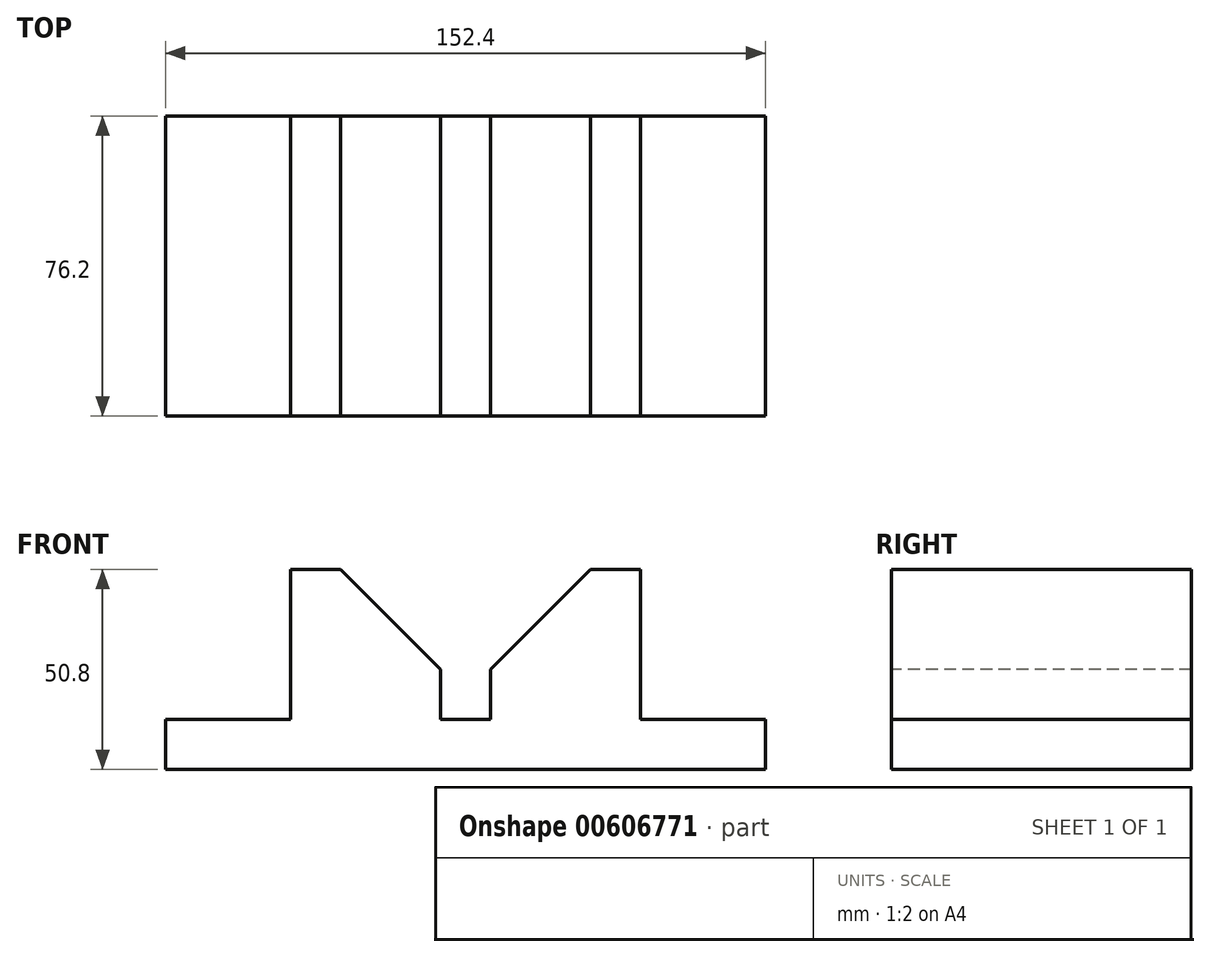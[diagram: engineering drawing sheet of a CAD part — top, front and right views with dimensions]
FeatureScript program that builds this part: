
annotation { "Feature Type Name" : "Feature", "Feature Type Description" : "" }
export const myFeature = defineFeature(function(context is Context, id is Id, definition is map)
    precondition{}
    {
        {
            var Q0;
            Q0=qCreatedBy(makeId("Front.planeOp"),FACE);
            var sketch = newSketch(context, id + "F0", { "sketchPlane" : qUnion([Q0])});
            skLineSegment(sketch, "E0", {"start": v(0, 0) * mm, "end": v(152.4, 0) * mm});
            skLineSegment(sketch, "E1", {"start": v(152.4, 0) * mm, "end": v(152.4, 50.8) * mm});
            skLineSegment(sketch, "E2", {"start": v(152.4, 50.8) * mm, "end": v(0, 50.8) * mm});
            skLineSegment(sketch, "E3", {"start": v(0, 50.8) * mm, "end": v(0, 0) * mm});
            skSolve(sketch);
        }
        {
            var Q0;
            Q0=makeQuery(id+"F0.imprint","IMPRINT",FACE,{"disambiguationData":[TD([[makeQuery(id+"F0.imprint","IMPRINT",EDGE,{"derivedFrom":sQuery(id+"F0.wireOp",EDGE,"E0")}),1.0]])]});
            extrude(context, id + "F1", {"entities" : qUnion([Q0]), "oppositeDirection" : true, "depth" : 76.2 * mm, "offsetDistance" : 25.4 * mm});
        }
        {
            var Q0;
            Q0=makeQuery(id+"F1.opExtrude","SWEPT_FACE",FACE,{"disambiguationData":[OSD([sQuery(id+"F0.wireOp",EDGE,"E2")])]});
            var sketch = newSketch(context, id + "F2", { "sketchPlane" : qUnion([Q0])});
            skLineSegment(sketch, "E4", {"start": v(31.75, 76.2) * mm, "end": v(31.75, 0) * mm});
            skLineSegment(sketch, "E5", {"start": v(31.75, 0) * mm, "end": v(0, 0) * mm});
            skLineSegment(sketch, "E6", {"start": v(0, 0) * mm, "end": v(0, 76.2) * mm});
            skLineSegment(sketch, "E7", {"start": v(0, 76.2) * mm, "end": v(31.75, 76.2) * mm});
            skLineSegment(sketch, "E8", {"start": v(120.65, 76.2) * mm, "end": v(120.65, 0) * mm});
            skLineSegment(sketch, "E9", {"start": v(120.65, 0) * mm, "end": v(152.4, 0) * mm});
            skLineSegment(sketch, "E10", {"start": v(152.4, 0) * mm, "end": v(152.4, 76.2) * mm});
            skLineSegment(sketch, "E11", {"start": v(152.4, 76.2) * mm, "end": v(120.65, 76.2) * mm});
            skSolve(sketch);
        }
        {
            var Q0;
            Q0 = qSketchRegion(id + "F2", true);
            extrude(context, id + "F3", {"entities" : qUnion([Q0]), "operationType" : NewBodyOperationType.REMOVE, "oppositeDirection" : true, "depth" : 38.1 * mm, "offsetDistance" : 25.4 * mm});
        }
        {
            var Q0;
            Q0=makeQuery(id+"F1.opExtrude","SWEPT_FACE",FACE,{"disambiguationData":[OSD([sQuery(id+"F0.wireOp",EDGE,"E2")])]});
            var sketch = newSketch(context, id + "F4", { "sketchPlane" : qUnion([Q0])});
            skLineSegment(sketch, "E12", {"start": v(69.85, 76.2) * mm, "end": v(69.85, 0) * mm});
            skLineSegment(sketch, "E13", {"start": v(69.85, 0) * mm, "end": v(82.55, 0) * mm});
            skLineSegment(sketch, "E14", {"start": v(82.55, 0) * mm, "end": v(82.55, 76.2) * mm});
            skLineSegment(sketch, "E15", {"start": v(82.55, 76.2) * mm, "end": v(69.85, 76.2) * mm});
            skLineSegment(sketch, "E16", {"start": v(82.55, 76.2) * mm, "end": v(120.65, 76.2) * mm});
            skLineSegment(sketch, "E17", {"start": v(31.75, 0) * mm, "end": v(69.85, 0) * mm});
            skLineSegment(sketch, "E18", {"start": v(82.55, 0) * mm, "end": v(120.65, 0) * mm});
            skSolve(sketch);
        }
        {
            var Q0;
            Q0 = qSketchRegion(id + "F4", true);
            extrude(context, id + "F5", {"entities" : qUnion([Q0]), "operationType" : NewBodyOperationType.REMOVE, "oppositeDirection" : true, "depth" : 38.1 * mm, "offsetDistance" : 25.4 * mm});
        }
        {
            var Q0;
            Q0=makeQuery(id+"F1.opExtrude","CAP_FACE",FACE,{"disambiguationData":[OSD([sQuery(id+"F0.wireOp",EDGE,"E0"),sQuery(id+"F0.wireOp",EDGE,"E1"),sQuery(id+"F0.wireOp",EDGE,"E2"),sQuery(id+"F0.wireOp",EDGE,"E3")])],"isStart":true});
            var sketch = newSketch(context, id + "F6", { "sketchPlane" : qUnion([Q0])});
            skLineSegment(sketch, "E19", {"start": v(69.85, 12.7) * mm, "end": v(69.85, 25.4) * mm});
            skLineSegment(sketch, "E20", {"start": v(69.85, 25.4) * mm, "end": v(44.45, 50.8) * mm});
            skLineSegment(sketch, "E21", {"start": v(44.45, 50.8) * mm, "end": v(31.75, 50.8) * mm});
            skLineSegment(sketch, "E22", {"start": v(31.75, 50.8) * mm, "end": v(31.75, 31.75) * mm});
            skLineSegment(sketch, "E23", {"start": v(31.75, 31.75) * mm, "end": v(31.75, 12.7) * mm});
            skLineSegment(sketch, "E24", {"start": v(31.75, 12.7) * mm, "end": v(69.85, 12.7) * mm});
            skLineSegment(sketch, "E25", {"start": v(44.45, 50.8) * mm, "end": v(69.85, 50.8) * mm});
            skLineSegment(sketch, "E26", {"start": v(69.85, 50.8) * mm, "end": v(69.85, 25.4) * mm});
            skSolve(sketch);
        }
        {
            var Q0;
            Q0=makeQuery(id+"F6.imprint","IMPRINT",FACE,{"disambiguationData":[TD([[makeQuery(id+"F6.imprint","IMPRINT",EDGE,{"derivedFrom":sQuery(id+"F6.wireOp",EDGE,"E20")}),-1.0]])]});
            extrude(context, id + "F7", {"entities" : qUnion([Q0]), "operationType" : NewBodyOperationType.REMOVE, "oppositeDirection" : true, "depth" : 76.2 * mm, "offsetDistance" : 25.4 * mm});
        }
        {
            var Q0;
            Q0=makeQuery(id+"F1.opExtrude","CAP_FACE",FACE,{"disambiguationData":[OSD([sQuery(id+"F0.wireOp",EDGE,"E0"),sQuery(id+"F0.wireOp",EDGE,"E1"),sQuery(id+"F0.wireOp",EDGE,"E2"),sQuery(id+"F0.wireOp",EDGE,"E3")])],"isStart":true});
            var sketch = newSketch(context, id + "F8", { "sketchPlane" : qUnion([Q0])});
            skLineSegment(sketch, "E27", {"start": v(82.55, 12.7) * mm, "end": v(82.55, 25.4) * mm});
            skLineSegment(sketch, "E28", {"start": v(120.65, 50.8) * mm, "end": v(120.65, 12.7) * mm});
            skLineSegment(sketch, "E29", {"start": v(120.65, 12.7) * mm, "end": v(82.55, 12.7) * mm});
            skLineSegment(sketch, "E30", {"start": v(82.55, 25.4) * mm, "end": v(82.55, 50.8) * mm});
            skLineSegment(sketch, "E31", {"start": v(82.55, 25.4) * mm, "end": v(107.95, 50.8) * mm});
            skLineSegment(sketch, "E32", {"start": v(107.95, 50.8) * mm, "end": v(120.65, 50.8) * mm});
            skLineSegment(sketch, "E33", {"start": v(107.95, 50.8) * mm, "end": v(82.55, 25.4) * mm});
            skSolve(sketch);
        }
        {
            var Q0;
            {var subQ0=sQuery(id+"F8.wireOp",EDGE,"E30");Q0=makeQuery(id+"F8.imprint","IMPRINT",FACE,{"disambiguationData":[TD([[makeQuery(id+"F8.imprint","IMPRINT",EDGE,{"derivedFrom":subQ0}),-1.0]])]});}
            extrude(context, id + "F9", {"entities" : qUnion([Q0]), "operationType" : NewBodyOperationType.REMOVE, "oppositeDirection" : true, "depth" : 76.2 * mm, "offsetDistance" : 25.4 * mm});
        }
    });
